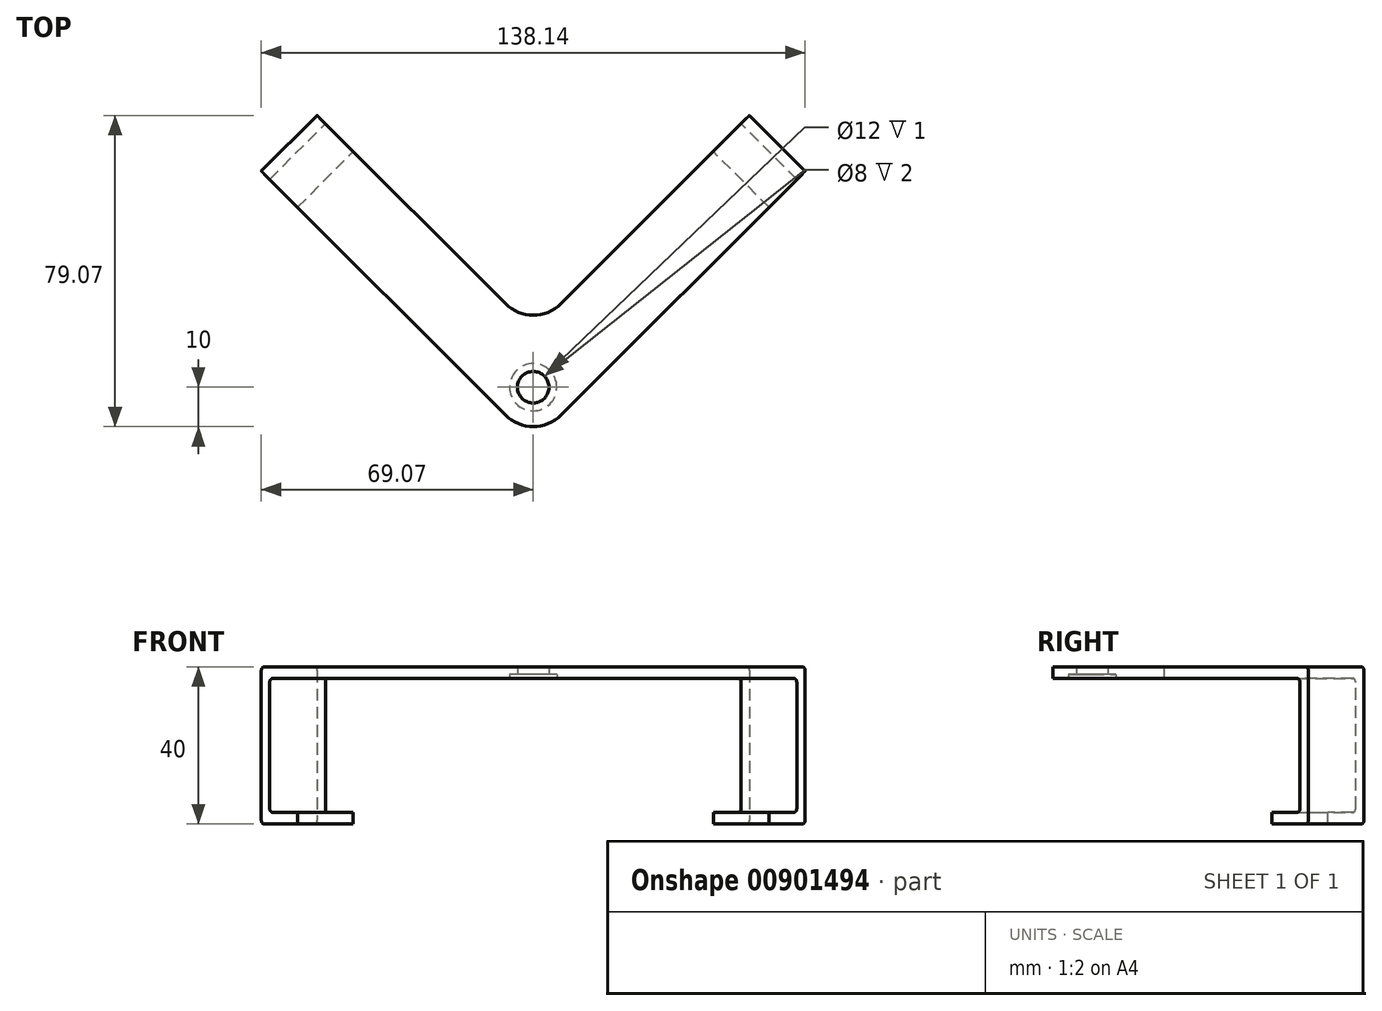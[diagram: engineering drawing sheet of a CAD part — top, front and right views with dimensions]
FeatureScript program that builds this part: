
annotation { "Feature Type Name" : "Feature", "Feature Type Description" : "" }
export const myFeature = defineFeature(function(context is Context, id is Id, definition is map)
    precondition{}
    {
        {
            var Q0;
            Q0=qCreatedBy(makeId("Top.planeOp"),FACE);
            var sketch = newSketch(context, id + "F0", { "sketchPlane" : qUnion([Q0])});
            skPoint(sketch, "E0.middle", {"position": v(0, 0) * mm});
            skCircle(sketch, "E1", {"center": v(0, 0) * mm, "radius": 4 * mm});
            skLineSegment(sketch, "E2", {"start": v(0, 124) * mm, "end": v(-124, 0) * mm, "construction": true});
            skLineSegment(sketch, "E3.MirrorCS", {"start": v(0, 124) * mm, "end": v(124, 0) * mm, "construction": true});
            skLineSegment(sketch, "E4.bottom", {"start": v(57.5, -34) * mm, "end": v(-57.5, -34) * mm, "construction": true});
            skLineSegment(sketch, "E4.top", {"start": v(57.5, 34) * mm, "end": v(-57.5, 34) * mm, "construction": true});
            skLineSegment(sketch, "E4.left", {"start": v(57.5, -34) * mm, "end": v(57.5, 34) * mm, "construction": true});
            skLineSegment(sketch, "E4.right", {"start": v(-57.5, -34) * mm, "end": v(-57.5, 34) * mm, "construction": true});
            skLineSegment(sketch, "E5", {"start": v(-54.93, 69.07) * mm, "end": v(0, 14.14) * mm});
            skPoint(sketch, "E5.endSnap0", {"position": v(0, 34) * mm});
            skLineSegment(sketch, "E6", {"start": v(-69.07, 54.93) * mm, "end": v(0, -14.14) * mm});
            skLineSegment(sketch, "E7", {"start": v(-69.07, 54.93) * mm, "end": v(-54.93, 69.07) * mm});
            skLineSegment(sketch, "E8.MirrorCS", {"start": v(54.93, 69.07) * mm, "end": v(0, 14.14) * mm});
            skLineSegment(sketch, "E9.MirrorCS", {"start": v(69.07, 54.93) * mm, "end": v(0, -14.14) * mm});
            skLineSegment(sketch, "E10", {"start": v(54.93, 69.07) * mm, "end": v(69.07, 54.93) * mm});
            skLineSegment(sketch, "E11", {"start": v(-59.88, 45.74) * mm, "end": v(-45.74, 59.88) * mm});
            skLineSegment(sketch, "E12.MirrorCS", {"start": v(59.88, 45.74) * mm, "end": v(45.74, 59.88) * mm});
            skLineSegment(sketch, "E13", {"start": v(-66.95, 52.8) * mm, "end": v(-52.8, 66.95) * mm});
            skLineSegment(sketch, "E14.MirrorCS", {"start": v(66.95, 52.8) * mm, "end": v(52.8, 66.95) * mm});
            skCircle(sketch, "E15", {"center": v(0, 0) * mm, "radius": 6 * mm});
            skSolve(sketch);
        }
        {
            var Q0;
            {var subQ0=sQuery(id+"F0.wireOp",EDGE,"E11");Q0=makeQuery(id+"F0.imprint","IMPRINT",FACE,{"disambiguationData":[TD([[makeQuery(id+"F0.imprint","IMPRINT",EDGE,{"derivedFrom":subQ0}),1.0]])]});}
            var Q1;
            Q1=makeQuery(id+"F0.imprint","IMPRINT",FACE,{"disambiguationData":[TD([[makeQuery(id+"F0.imprint","IMPRINT",EDGE,{"derivedFrom":sQuery(id+"F0.wireOp",EDGE,"E1")}),1.0]])]});
            var Q2;
            {var subQ0=sQuery(id+"F0.wireOp",EDGE,"E7");Q2=makeQuery(id+"F0.imprint","IMPRINT",FACE,{"disambiguationData":[TD([[makeQuery(id+"F0.imprint","IMPRINT",EDGE,{"derivedFrom":subQ0}),-1.0]])]});}
            var Q3;
            Q3=makeQuery(id+"F0.imprint","IMPRINT",FACE,{"disambiguationData":[TD([[makeQuery(id+"F0.imprint","IMPRINT",EDGE,{"derivedFrom":sQuery(id+"F0.wireOp",EDGE,"E1")}),-1.0]])]});
            var Q4;
            {var subQ0=sQuery(id+"F0.wireOp",EDGE,"E12.MirrorCS");Q4=makeQuery(id+"F0.imprint","IMPRINT",FACE,{"disambiguationData":[TD([[makeQuery(id+"F0.imprint","IMPRINT",EDGE,{"derivedFrom":subQ0}),-1.0]])]});}
            var Q5;
            {var subQ0=sQuery(id+"F0.wireOp",EDGE,"E10");Q5=makeQuery(id+"F0.imprint","IMPRINT",FACE,{"disambiguationData":[TD([[makeQuery(id+"F0.imprint","IMPRINT",EDGE,{"derivedFrom":subQ0}),-1.0]])]});}
            var Q6;
            {var subQ7=sQuery(id+"F0.wireOp",EDGE,"E11");Q6=makeQuery(id+"F0.imprint","IMPRINT",FACE,{"disambiguationData":[TD([[makeQuery(id+"F0.imprint","IMPRINT",EDGE,{"derivedFrom":subQ7}),-1.0]])]});}
            extrude(context, id + "F1", {"entities" : qUnion([Q0, Q1, Q2, Q3, Q4, Q5, Q6]), "depth" : 3 * mm, "offsetDistance" : 25 * mm});
        }
        {
            var Q0;
            {var subQ0=sQuery(id+"F0.wireOp",EDGE,"E7");Q0=makeQuery(id+"F0.imprint","IMPRINT",FACE,{"disambiguationData":[TD([[makeQuery(id+"F0.imprint","IMPRINT",EDGE,{"derivedFrom":subQ0}),-1.0]])]});}
            var Q1;
            {var subQ0=sQuery(id+"F0.wireOp",EDGE,"E11");Q1=makeQuery(id+"F0.imprint","IMPRINT",FACE,{"disambiguationData":[TD([[makeQuery(id+"F0.imprint","IMPRINT",EDGE,{"derivedFrom":subQ0}),1.0]])]});}
            var Q2;
            {var subQ0=sQuery(id+"F0.wireOp",EDGE,"E12.MirrorCS");Q2=makeQuery(id+"F0.imprint","IMPRINT",FACE,{"disambiguationData":[TD([[makeQuery(id+"F0.imprint","IMPRINT",EDGE,{"derivedFrom":subQ0}),-1.0]])]});}
            var Q3;
            {var subQ0=sQuery(id+"F0.wireOp",EDGE,"E10");Q3=makeQuery(id+"F0.imprint","IMPRINT",FACE,{"disambiguationData":[TD([[makeQuery(id+"F0.imprint","IMPRINT",EDGE,{"derivedFrom":subQ0}),-1.0]])]});}
            extrude(context, id + "F2", {"entities" : qUnion([Q0, Q1, Q2, Q3]), "operationType" : NewBodyOperationType.ADD, "depth" : -37 * mm, "offsetDistance" : 25 * mm});
        }
        {
            var Q0;
            {var subQ0=sQuery(id+"F0.wireOp",EDGE,"E11");Q0=makeQuery(id+"F0.imprint","IMPRINT",FACE,{"disambiguationData":[TD([[makeQuery(id+"F0.imprint","IMPRINT",EDGE,{"derivedFrom":subQ0}),1.0]])]});}
            var Q1;
            {var subQ0=sQuery(id+"F0.wireOp",EDGE,"E12.MirrorCS");Q1=makeQuery(id+"F0.imprint","IMPRINT",FACE,{"disambiguationData":[TD([[makeQuery(id+"F0.imprint","IMPRINT",EDGE,{"derivedFrom":subQ0}),-1.0]])]});}
            extrude(context, id + "F3", {"entities" : qUnion([Q0, Q1]), "operationType" : NewBodyOperationType.REMOVE, "oppositeDirection" : true, "depth" : 34 * mm, "offsetDistance" : 25 * mm});
        }
        {
            var Q0;
            Q0=makeQuery(id+"F0.imprint","IMPRINT",FACE,{"disambiguationData":[TD([[makeQuery(id+"F0.imprint","IMPRINT",EDGE,{"derivedFrom":sQuery(id+"F0.wireOp",EDGE,"E1")}),-1.0]])]});
            extrude(context, id + "F4", {"entities" : qUnion([Q0]), "operationType" : NewBodyOperationType.REMOVE, "depth" : 1 * mm, "offsetDistance" : 25 * mm});
        }
        {
            var Q0;
            Q0=makeQuery(id+"F0.imprint","IMPRINT",FACE,{"disambiguationData":[TD([[makeQuery(id+"F0.imprint","IMPRINT",EDGE,{"derivedFrom":sQuery(id+"F0.wireOp",EDGE,"E1")}),1.0]])]});
            extrude(context, id + "F5", {"entities" : qUnion([Q0]), "operationType" : NewBodyOperationType.REMOVE, "oppositeDirection" : true, "depth" : -5000 * mm, "offsetDistance" : 25 * mm});
        }
        {
            var Q0;
            Q0=makeQuery(id+"F1.opExtrude","SWEPT_EDGE",EDGE,{"disambiguationData":[OSD([sQuery(id+"F0.wireOp",EDGE,"E6"),sQuery(id+"F0.wireOp",EDGE,"E9.MirrorCS")])]});
            var Q1;
            Q1=makeQuery(id+"F1.opExtrude","SWEPT_EDGE",EDGE,{"disambiguationData":[OSD([sQuery(id+"F0.wireOp",EDGE,"E5"),sQuery(id+"F0.wireOp",EDGE,"E8.MirrorCS")])]});
            fillet(context, id + "F6", {"entities" : qUnion([Q0, Q1]), "radius" : 10 * mm, "tangentPropagation" : true, "allowEdgeOverflow" : false});
        }
        {
            var Q0;
            Q0=makeQuery(id+"F1.opExtrude","CAP_EDGE",EDGE,{"disambiguationData":[OSD([sQuery(id+"F0.wireOp",EDGE,"E10")])],"isStart":false});
            var Q1;
            Q1=makeQuery(id+"F3.boolean.opBoolean","COPY",EDGE,{"derivedFrom":makeQuery(id+"F3.opExtrude","CAP_EDGE",EDGE,{"disambiguationData":[OSD([sQuery(id+"F0.wireOp",EDGE,"E14.MirrorCS")])],"isStart":true})});
            var Q2;
            Q2=makeQuery(id+"F2.opExtrude","CAP_EDGE",EDGE,{"disambiguationData":[OSD([sQuery(id+"F0.wireOp",EDGE,"E10")])],"isStart":false});
            var Q3;
            Q3=makeQuery(id+"F3.boolean.opBoolean","COPY",EDGE,{"derivedFrom":makeQuery(id+"F3.opExtrude","CAP_EDGE",EDGE,{"disambiguationData":[OSD([sQuery(id+"F0.wireOp",EDGE,"E14.MirrorCS")])],"isStart":false})});
            var Q4;
            Q4=makeQuery(id+"F2.opExtrude","CAP_EDGE",EDGE,{"disambiguationData":[OSD([sQuery(id+"F0.wireOp",EDGE,"E7")])],"isStart":false});
            var Q5;
            Q5=makeQuery(id+"F1.opExtrude","CAP_EDGE",EDGE,{"disambiguationData":[OSD([sQuery(id+"F0.wireOp",EDGE,"E7")])],"isStart":false});
            var Q6;
            Q6=makeQuery(id+"F3.boolean.opBoolean","COPY",EDGE,{"derivedFrom":makeQuery(id+"F3.opExtrude","CAP_EDGE",EDGE,{"disambiguationData":[OSD([sQuery(id+"F0.wireOp",EDGE,"E13")])],"isStart":true})});
            var Q7;
            Q7=makeQuery(id+"F3.boolean.opBoolean","COPY",EDGE,{"derivedFrom":makeQuery(id+"F3.opExtrude","CAP_EDGE",EDGE,{"disambiguationData":[OSD([sQuery(id+"F0.wireOp",EDGE,"E13")])],"isStart":false})});
            fillet(context, id + "F7", {"entities" : qUnion([Q0, Q1, Q2, Q3, Q4, Q5, Q6, Q7]), "radius" : 1 * mm, "tangentPropagation" : true, "allowEdgeOverflow" : false});
        }
    });
